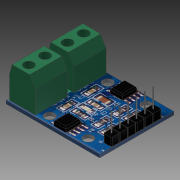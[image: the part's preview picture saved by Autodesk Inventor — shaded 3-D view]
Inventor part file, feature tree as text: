
AUTODESK INVENTOR PART (.ipt)
format: ipt  version: 2015 (Build 190159000, 159)  size: 780,800 bytes
history: native  units: mm
features: sketch x13, chamfer x12, extrude x9, projected_geometry x6, other x3, pattern_linear x2, hole x1, mirror x1, sweep x1
ambient origin geometry x8: Origin, YZ Plane, XZ Plane, XY Plane, X Axis, Y Axis, Z Axis, Center Point
bodies: Body1 (feature_tree), Body2 (feature_tree), Body3 (feature_tree)
feature tree (48):
  other  "솔리드1"
  extrude  "돌출1"  Depth=29.0mm
  hole  "구멍1"  [1 undecoded]
  pattern_linear  "직사각형 패턴1"  Spacing1=1.0mm  [1 undecoded]
  extrude  "돌출2"  Depth=6.0mm
  chamfer  "모따기1"  Distance=9.0mm
  extrude  "돌출3"  Depth=20.0mm
  chamfer  "모따기2"  Distance=20.0mm
  pattern_linear  "직사각형 패턴2"  Spacing1=2.5mm  [1 undecoded]
  extrude  "돌출4"  Depth=15.5mm
  extrude  "돌출5"  Depth=2.5mm
  chamfer  "모따기3"  Distance=2.6mm
  chamfer  "모따기4"  Distance=2.5mm
  chamfer  "모따기5"  Distance=0.2mm Angle=45.0deg
  chamfer  "모따기6"  Distance=0.2mm
  chamfer  "모따기7"  Distance=0.2mm
  chamfer  "모따기8"  Distance=6.0mm
  chamfer  "모따기9"  Distance=2.0mm Angle=45.0deg
  chamfer  "모따기10"  Distance=2.6mm
  extrude  "돌출6"  Depth=15.5mm
  chamfer  "모따기11"  Distance=2.4mm
  chamfer  "모따기12"  Distance=4.5mm
  mirror  "대칭1"
  other  "전사1"
  extrude  "돌출8"  Depth=3.7mm
  sketch  "스케치9"
  extrude  "돌출9"  Depth=11.0mm
  extrude  "돌출10"  Depth=0.5mm
  sweep  "스윕1"
  sketch  "스케치1"
  sketch  "스케치2"
  sketch  "스케치3"
  sketch  "스케치4"
  projected_geometry  "투영된 루프1"
  sketch  "스케치5"
  sketch  "스케치6"
  sketch  "스케치7"
  sketch  "스케치8"
  projected_geometry  "투영된 루프2"
  other  "이미지1"
  sketch  "스케치10"
  sketch  "스케치11"
  projected_geometry  "투영된 루프3"
  projected_geometry  "투영된 루프4"
  projected_geometry  "투영된 루프5"
  projected_geometry  "투영된 루프6"
  sketch  "스케치12"
  sketch  "스케치13"
note: 3 required parameter values undecoded (feature->parameter linkage not recoverable at this tier; creation-order binding heuristic only, values carry confidence <= 0.55)
